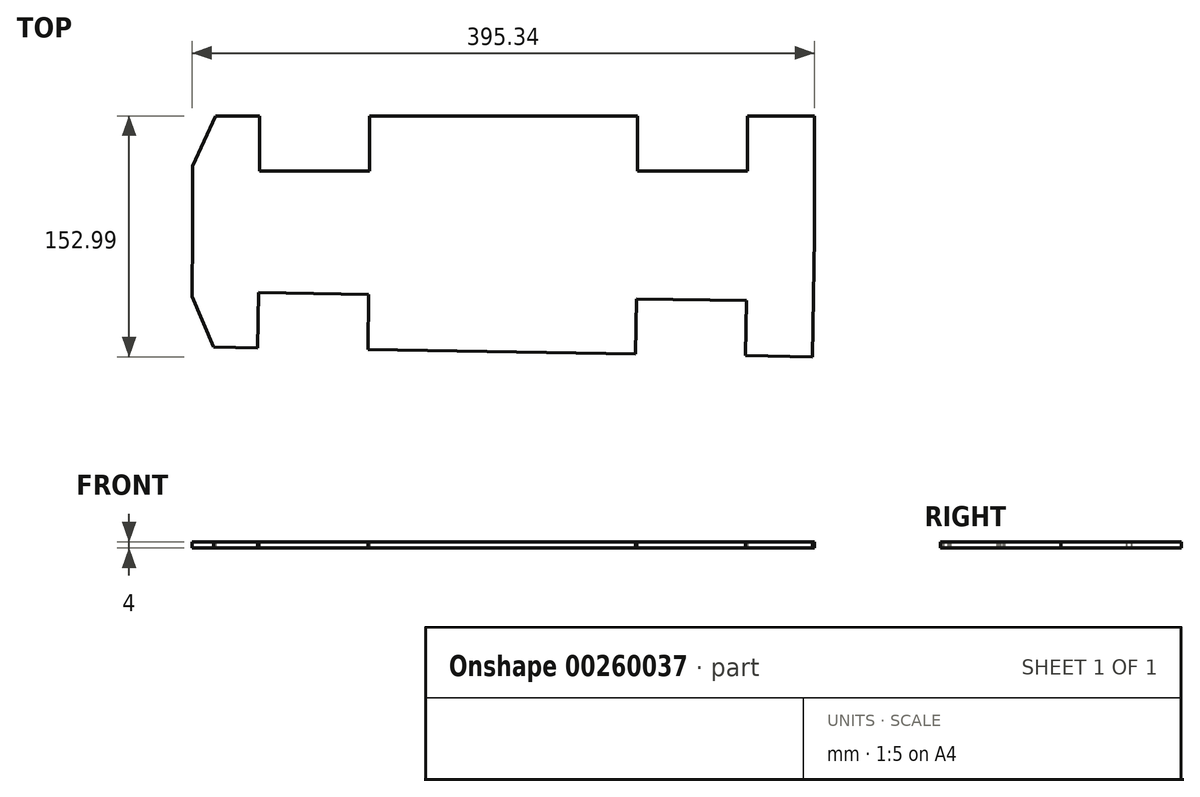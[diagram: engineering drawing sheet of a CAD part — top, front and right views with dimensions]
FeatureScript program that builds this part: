
annotation { "Feature Type Name" : "Feature", "Feature Type Description" : "" }
export const myFeature = defineFeature(function(context is Context, id is Id, definition is map)
    precondition{}
    {
        {
            var Q0;
            Q0=qCreatedBy(makeId("Top.planeOp"),FACE);
            var sketch = newSketch(context, id + "F0", { "sketchPlane" : qUnion([Q0])});
            skLineSegment(sketch, "E0", {"start": v(0, 0) * mm, "end": v(0, 35) * mm});
            skLineSegment(sketch, "E1", {"start": v(0, 35) * mm, "end": v(-170, 35) * mm});
            skLineSegment(sketch, "E2", {"start": v(-170, 35) * mm, "end": v(-170, 0) * mm});
            skLineSegment(sketch, "E3", {"start": v(0, 0) * mm, "end": v(70, 0) * mm});
            skLineSegment(sketch, "E4", {"start": v(70, 0) * mm, "end": v(70, 35) * mm});
            skLineSegment(sketch, "E5", {"start": v(70, 35) * mm, "end": v(112.5, 35) * mm});
            skLineSegment(sketch, "E6", {"start": v(112.5, 35) * mm, "end": v(112.5, -41.5) * mm});
            skLineSegment(sketch, "E7", {"start": v(-170, 0) * mm, "end": v(-240, 0) * mm});
            skLineSegment(sketch, "E8", {"start": v(-240, 0) * mm, "end": v(-240, 35) * mm});
            skLineSegment(sketch, "E9", {"start": v(-240, 35) * mm, "end": v(-267.88, 35) * mm});
            skLineSegment(sketch, "E10", {"start": v(-267.88, 35) * mm, "end": v(-282.5, 3.2) * mm});
            skLineSegment(sketch, "E11", {"start": v(-282.5, 3.2) * mm, "end": v(-282.5, -38.3) * mm});
            skPoint(sketch, "E12.orphan", {"position": v(-282.5, 35) * mm});
            skPoint(sketch, "E13.MirrorP", {"position": v(-283.69, -111.59) * mm});
            skLineSegment(sketch, "E14.MirrorCS", {"start": v(-0.66, -81.17) * mm, "end": v(-1.23, -116.17) * mm});
            skLineSegment(sketch, "E15.MirrorCS", {"start": v(-1.23, -116.17) * mm, "end": v(-171.2, -113.41) * mm});
            skLineSegment(sketch, "E16.MirrorCS", {"start": v(-171.2, -113.41) * mm, "end": v(-170.64, -78.42) * mm});
            skLineSegment(sketch, "E17.MirrorCS", {"start": v(-0.66, -81.17) * mm, "end": v(69.33, -82.3) * mm});
            skLineSegment(sketch, "E18.MirrorCS", {"start": v(69.33, -82.3) * mm, "end": v(68.77, -117.3) * mm});
            skLineSegment(sketch, "E19.MirrorCS", {"start": v(68.77, -117.3) * mm, "end": v(111.26, -117.99) * mm});
            skLineSegment(sketch, "E20.MirrorCS", {"start": v(111.26, -117.99) * mm, "end": v(112.5, -41.5) * mm});
            skLineSegment(sketch, "E21.MirrorCS", {"start": v(-170.64, -78.42) * mm, "end": v(-240.63, -77.28) * mm});
            skLineSegment(sketch, "E22.MirrorCS", {"start": v(-241.2, -112.28) * mm, "end": v(-269.07, -111.82) * mm});
            skLineSegment(sketch, "E23.MirrorCS", {"start": v(-240.63, -77.28) * mm, "end": v(-241.2, -112.28) * mm});
            skLineSegment(sketch, "E24", {"start": v(-282.5, -38.3) * mm, "end": v(-282.84, -79.8) * mm});
            skLineSegment(sketch, "E25", {"start": v(-282.84, -79.8) * mm, "end": v(-269.07, -111.82) * mm});
            skSolve(sketch);
        }
        {
            var Q0;
            Q0 = qSketchRegion(id + "F0", true);
            extrude(context, id + "F1", {"entities" : qUnion([Q0]), "depth" : 4 * mm});
        }
    });
